# Revit family: 34-80-001 DN50-400
name_source: partatom
category: Pipe Accessories
units: mm (PartAtom-declared; Revit-internal decimal feet)

## family parameters
Always vertical = No
Cut with Voids When Loaded = No
Part Type = Valve - Breaks Into
Round Connector Dimension = Use Diameter
Shared = No
Work Plane-Based = No

## types (22) — shared parameters
1 = 1 mm  [stored 0.00328084 ft]
10 = 10 mm  [stored 0.0328084 ft]
104 = 104 mm
105 = 105 mm  [stored 0.344488 ft]
115 = 125 mm  [stored 0.410105 ft]
15 = 15 mm  [stored 0.0492126 ft]
156 = 78 mm  [stored 0.255906 ft]
177 = 177 mm  [stored 0.580709 ft]
2 = 2 mm  [stored 0.00656168 ft]
20 = 20 mm  [stored 0.0656168 ft]
25 = 25 mm  [stored 0.082021 ft]
30 = 30 mm  [stored 0.0984252 ft]
330 = 330 mm
360 = 360 mm
40 = 40 mm  [stored 0.131234 ft]
5 = 5 mm  [stored 0.0164042 ft]
52.5 = 52.5 mm  [stored 0.172244 ft]
55 = 55 mm  [stored 0.180446 ft]
56 = 28 mm  [stored 0.0918635 ft]
66 = 33 mm  [stored 0.108268 ft]
7 = 7 mm  [stored 0.0229659 ft]
70 = 70 mm  [stored 0.229659 ft]
8 = 8 mm  [stored 0.0262467 ft]
Body_H = 468 mm
DN050_stem length 250 = 34-050-80-00010010
DN065_stem length 250 = 34-065-80-00010010
DN080_stem length 250 = 34-080-80-00010010
DN100_stem length 1250 = 34-100-80-02010010
DN100_stem length 250 = 34-100-80-00010010
DN100_stem length 750 = 34-100-80-01010010
DN150_stem length 1250 = 34-150-80-02010010
DN150_stem length 250 = 34-150-80-00010010
DN150_stem length 750 = 34-150-80-01010010
DN200_stem length 1250 = 34-200-80-02010010
DN200_stem length 250 = 34-200-80-00010010
DN200_stem length 750 = 34-200-80-01010010
DN250_stem length 1250 = 34-250-80-02010010
DN250_stem length 250 = 34-250-80-00010010
DN250_stem length 750 = 34-250-80-01010010
DN300_stem length 1250 = 34-300-80-02010010
DN300_stem length 250 = 34-300-80-00010010
DN300_stem length 750 = 34-300-80-01010010
DN350_stem length 1250 = 34-350-80-02010010
DN350_stem length 250 = 34-350-80-00010010
DN350_stem length 750 = 34-350-80-01010010
DN400_stem length 750 = 34-400-80-01010010
Description_ = AVK WALL POST INDICATOR
FL_T = 19 mm  [stored 0.062336 ft]
FL_dia = 152.5 mm  [stored 0.500328 ft]
Fillet = 15 mm  [stored 0.0492126 ft]
Handwheel_dia = 180 mm  [stored 0.590551 ft]
Handwheel_dia1 = 153 mm  [stored 0.501969 ft]
Search_table = 34-80-001 DN50-400
URL product pages = https://www.avkvalves.com
eye_bolt_H = 44 mm  [stored 0.144357 ft]
eye_bolt_dim1 = 30 mm  [stored 0.0984252 ft]
zero-valued in all types: Default Elevation

## per-type parameters (varying)
| type | DN | Stem_length | Stem_length1 |
| DN050_stem length 250 | 50 mm  [stored 0.164042 ft] | 250 mm  [stored 0.82021 ft] | 0 mm  [stored 0 ft] |
| DN065_stem length 250 | 65 mm  [stored 0.213255 ft] | 250 mm  [stored 0.82021 ft] | 0 mm  [stored 0 ft] |
| DN080_stem length 250 | 80 mm  [stored 0.262467 ft] | 250 mm  [stored 0.82021 ft] | 0 mm  [stored 0 ft] |
| DN100_stem length 250 | 100 mm  [stored 0.328084 ft] | 250 mm  [stored 0.82021 ft] | 0 mm  [stored 0 ft] |
| DN100_stem length 750 | 100.1 mm  [stored 0.328412 ft] | 750 mm | 500 mm |
| DN100_stem length 1250 | 100.2 mm  [stored 0.32874 ft] | 1250 mm | 1000 mm |
| DN150_stem length 250 | 150 mm  [stored 0.492126 ft] | 250 mm  [stored 0.82021 ft] | 0 mm  [stored 0 ft] |
| DN150_stem length 750 | 150.1 mm  [stored 0.492454 ft] | 750 mm | 500 mm |
| DN150_stem length 1250 | 150.2 mm  [stored 0.492782 ft] | 1250 mm | 1000 mm |
| DN200_stem length 250 | 200 mm  [stored 0.656168 ft] | 250 mm  [stored 0.82021 ft] | 0 mm  [stored 0 ft] |
| DN200_stem length 750 | 200.1 mm  [stored 0.656496 ft] | 750 mm | 500 mm |
| DN200_stem length 1250 | 200.2 mm  [stored 0.656824 ft] | 1250 mm | 1000 mm |
| DN250_stem length 250 | 250 mm  [stored 0.82021 ft] | 250 mm  [stored 0.82021 ft] | 0 mm  [stored 0 ft] |
| DN250_stem length 750 | 250.1 mm | 750 mm | 500 mm |
| DN250_stem length 1250 | 250.2 mm | 1250 mm | 1000 mm |
| DN300_stem length 250 | 300 mm | 250 mm  [stored 0.82021 ft] | 0 mm  [stored 0 ft] |
| DN300_stem length 750 | 300.1 mm | 750 mm | 500 mm |
| DN300_stem length 1250 | 300.2 mm | 1250 mm | 1000 mm |
| DN350_stem length 250 | 350 mm | 250 mm  [stored 0.82021 ft] | 0 mm  [stored 0 ft] |
| DN350_stem length 750 | 350.1 mm | 750 mm | 500 mm |
| DN350_stem length 1250 | 350.2 mm | 1250 mm | 1000 mm |
| DN400_stem length 750 | 400 mm | 750 mm | 500 mm |

note: [stored X ft] marks values corroborated as IEEE doubles in the binary element streams (Revit-internal decimal feet)

## geometry (parser evidence)
native form markers: Sweep x10
no freeform markers — native parametric forms only
